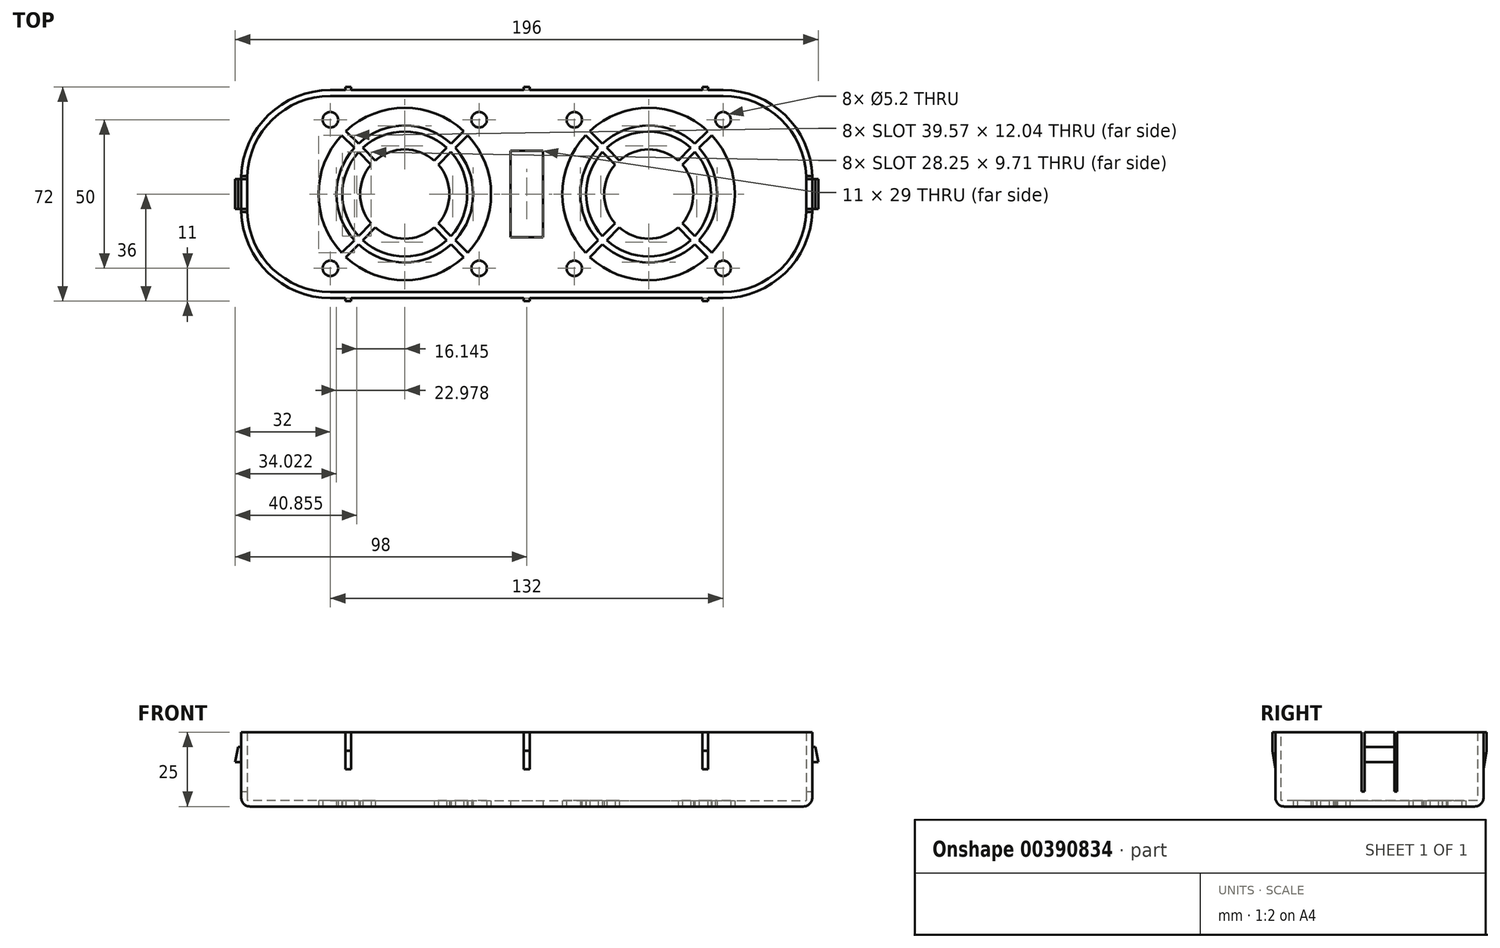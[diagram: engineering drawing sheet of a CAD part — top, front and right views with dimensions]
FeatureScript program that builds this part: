
annotation { "Feature Type Name" : "Feature", "Feature Type Description" : "" }
export const myFeature = defineFeature(function(context is Context, id is Id, definition is map)
    precondition{}
    {
        {
            var Q0;
            Q0=qCreatedBy(makeId("Top.planeOp"),FACE);
            var sketch = newSketch(context, id + "F0", { "sketchPlane" : qUnion([Q0])});
            skLineSegment(sketch, "E0", {"start": v(-96, 0) * mm, "end": v(96, 0) * mm, "construction": true});
            skLineSegment(sketch, "E1", {"start": v(0, 35) * mm, "end": v(0, -35) * mm, "construction": true});
            skLineSegment(sketch, "E2", {"start": v(-96, 5) * mm, "end": v(-96, -5) * mm});
            skArc(sketch, "E3", {"start": v(-96, 5) * mm, "mid": v(-87.21, 26.21) * mm, "end": v(-66, 35) * mm});
            skArc(sketch, "E4", {"start": v(-96, -5) * mm, "mid": v(-87.21, -26.21) * mm, "end": v(-66, -35) * mm});
            skLineSegment(sketch, "E5", {"start": v(96, 5) * mm, "end": v(96, -5) * mm});
            skArc(sketch, "E6", {"start": v(96, 5) * mm, "mid": v(87.21, 26.21) * mm, "end": v(66, 35) * mm});
            skArc(sketch, "E7", {"start": v(96, -5) * mm, "mid": v(87.21, -26.21) * mm, "end": v(66, -35) * mm});
            skLineSegment(sketch, "E8", {"start": v(-66, 35) * mm, "end": v(66, 35) * mm});
            skLineSegment(sketch, "E9", {"start": v(-66, -35) * mm, "end": v(66, -35) * mm});
            skSolve(sketch);
        }
        {
            var Q0;
            Q0 = qSketchRegion(id + "F0", true);
            extrude(context, id + "F1", {"entities" : qUnion([Q0]), "depth" : 25 * mm});
        }
        {
            var Q0;
            Q0=makeQuery(id+"F1.opExtrude","CAP_FACE",FACE,{"disambiguationData":[OSD([sQuery(id+"F0.wireOp",EDGE,"E2"),sQuery(id+"F0.wireOp",EDGE,"E3"),sQuery(id+"F0.wireOp",EDGE,"E4"),sQuery(id+"F0.wireOp",EDGE,"E5"),sQuery(id+"F0.wireOp",EDGE,"E6"),sQuery(id+"F0.wireOp",EDGE,"E7"),sQuery(id+"F0.wireOp",EDGE,"E8"),sQuery(id+"F0.wireOp",EDGE,"E9")])],"isStart":false});
            shell(context, id + "F2", {"entities" : qUnion([Q0]), "thickness" : 2 * mm});
        }
        {
            var Q0;
            Q0=makeQuery(id+"F1.opExtrude","SWEPT_FACE",FACE,{"disambiguationData":[OSD([sQuery(id+"F0.wireOp",EDGE,"E5")])]});
            var sketch = newSketch(context, id + "F3", { "sketchPlane" : qUnion([Q0])});
            skLineSegment(sketch, "E10", {"start": v(-5, 25) * mm, "end": v(-5, 5) * mm});
            skLineSegment(sketch, "E11", {"start": v(5, 5) * mm, "end": v(5, 25) * mm});
            skLineSegment(sketch, "E12", {"start": v(5, 25) * mm, "end": v(6, 25) * mm});
            skLineSegment(sketch, "E13", {"start": v(6, 25) * mm, "end": v(6, 5) * mm});
            skLineSegment(sketch, "E14", {"start": v(6, 5) * mm, "end": v(5, 5) * mm});
            skLineSegment(sketch, "E15", {"start": v(-5, 25) * mm, "end": v(-6, 25) * mm});
            skLineSegment(sketch, "E16", {"start": v(-6, 25) * mm, "end": v(-6, 5) * mm});
            skLineSegment(sketch, "E17", {"start": v(-6, 5) * mm, "end": v(-5, 5) * mm});
            skSolve(sketch);
        }
        {
            var Q0;
            Q0 = qSketchRegion(id + "F3", true);
            extrude(context, id + "F4", {"entities" : qUnion([Q0]), "operationType" : NewBodyOperationType.REMOVE, "endBound" : BoundingType.THROUGH_ALL, "oppositeDirection" : true, "depth" : 25 * mm});
        }
        {
            var Q0;
            Q0=makeQuery(id+"F1.opExtrude","SWEPT_FACE",FACE,{"disambiguationData":[OSD([sQuery(id+"F0.wireOp",EDGE,"E5")])]});
            var sketch = newSketch(context, id + "F5", { "sketchPlane" : qUnion([Q0])});
            skLineSegment(sketch, "E18.bottom", {"start": v(-5, 20) * mm, "end": v(5, 20) * mm});
            skLineSegment(sketch, "E18.top", {"start": v(-5, 15) * mm, "end": v(5, 15) * mm});
            skLineSegment(sketch, "E18.left", {"start": v(-5, 20) * mm, "end": v(-5, 15) * mm});
            skLineSegment(sketch, "E18.right", {"start": v(5, 20) * mm, "end": v(5, 15) * mm});
            skSolve(sketch);
        }
        {
            var Q0;
            Q0 = qSketchRegion(id + "F5", true);
            extrude(context, id + "F6", {"entities" : qUnion([Q0]), "operationType" : NewBodyOperationType.ADD, "depth" : 2 * mm});
        }
        {
            var Q0;
            {var subQ0=sQuery(id+"F0.wireOp",EDGE,"E5");Q0=makeQuery(id+"F6.boolean.opBoolean","MERGE",FACE,{"derivedFrom":[makeQuery(id+"F4.boolean.opBoolean","COPY",FACE,{"disambiguationData":[TD([makeQuery(id+"F1.opExtrude","SWEPT_FACE",FACE,{"disambiguationData":[OSD([subQ0])]})])],"derivedFrom":makeQuery(id+"F4.opExtrude","SWEPT_FACE",FACE,{"disambiguationData":[OSD([sQuery(id+"F3.wireOp",EDGE,"E10")])]})}),makeQuery(id+"F6.opExtrude","SWEPT_FACE",FACE,{"disambiguationData":[OSD([sQuery(id+"F5.wireOp",EDGE,"E18.left")])]})]});}
            var sketch = newSketch(context, id + "F7", { "sketchPlane" : qUnion([Q0])});
            skLineSegment(sketch, "E19", {"start": v(98, 15) * mm, "end": v(97, 20) * mm});
            skLineSegment(sketch, "E20", {"start": v(97, 20) * mm, "end": v(98, 20) * mm});
            skLineSegment(sketch, "E21", {"start": v(98, 20) * mm, "end": v(98, 15) * mm});
            skSolve(sketch);
        }
        {
            var Q0;
            Q0 = qSketchRegion(id + "F7", true);
            extrude(context, id + "F8", {"entities" : qUnion([Q0]), "operationType" : NewBodyOperationType.REMOVE, "endBound" : BoundingType.THROUGH_ALL, "oppositeDirection" : true, "depth" : 25 * mm});
        }
        {
            var Q0;
            Q0=makeQuery(id+"F1.opExtrude","SWEPT_FACE",FACE,{"disambiguationData":[OSD([sQuery(id+"F0.wireOp",EDGE,"E2")])]});
            var sketch = newSketch(context, id + "F9", { "sketchPlane" : qUnion([Q0])});
            skLineSegment(sketch, "E22.bottom", {"start": v(-5, 20) * mm, "end": v(5, 20) * mm});
            skLineSegment(sketch, "E22.left", {"start": v(-5, 20) * mm, "end": v(-5, 15) * mm});
            skLineSegment(sketch, "E23", {"start": v(-5, 15) * mm, "end": v(5, 15) * mm});
            skLineSegment(sketch, "E24", {"start": v(5, 15) * mm, "end": v(5, 20) * mm});
            skSolve(sketch);
        }
        {
            var Q0;
            Q0 = qSketchRegion(id + "F9", true);
            extrude(context, id + "F10", {"entities" : qUnion([Q0]), "operationType" : NewBodyOperationType.ADD, "depth" : 2 * mm});
        }
        {
            var Q0;
            {var subQ0=sQuery(id+"F0.wireOp",EDGE,"E2");Q0=makeQuery(id+"F10.boolean.opBoolean","MERGE",FACE,{"derivedFrom":[makeQuery(id+"F4.boolean.opBoolean","COPY",FACE,{"disambiguationData":[TD([makeQuery(id+"F1.opExtrude","SWEPT_FACE",FACE,{"disambiguationData":[OSD([subQ0])]})])],"derivedFrom":makeQuery(id+"F4.opExtrude","SWEPT_FACE",FACE,{"disambiguationData":[OSD([sQuery(id+"F3.wireOp",EDGE,"E11")])]})}),makeQuery(id+"F10.opExtrude","SWEPT_FACE",FACE,{"disambiguationData":[OSD([sQuery(id+"F9.wireOp",EDGE,"E22.left")])]})]});}
            var sketch = newSketch(context, id + "F11", { "sketchPlane" : qUnion([Q0])});
            skLineSegment(sketch, "E25", {"start": v(98, 15) * mm, "end": v(97, 20) * mm});
            skLineSegment(sketch, "E26", {"start": v(97, 20) * mm, "end": v(98, 20) * mm});
            skLineSegment(sketch, "E27", {"start": v(98, 20) * mm, "end": v(98, 15) * mm});
            skSolve(sketch);
        }
        {
            var Q0;
            Q0 = qSketchRegion(id + "F11", true);
            extrude(context, id + "F12", {"entities" : qUnion([Q0]), "operationType" : NewBodyOperationType.REMOVE, "endBound" : BoundingType.THROUGH_ALL, "oppositeDirection" : true, "depth" : 25 * mm});
        }
        {
            var Q0;
            Q0=makeQuery(id+"F1.opExtrude","SWEPT_FACE",FACE,{"disambiguationData":[OSD([sQuery(id+"F0.wireOp",EDGE,"E8")])]});
            var sketch = newSketch(context, id + "F13", { "sketchPlane" : qUnion([Q0])});
            skPoint(sketch, "E28.oppositeSnap0", {"position": v(-66, 12.5) * mm});
            skLineSegment(sketch, "E28.bottom", {"start": v(-61, 25) * mm, "end": v(-59, 25) * mm});
            skLineSegment(sketch, "E28.top", {"start": v(-61, 12.5) * mm, "end": v(-59, 12.5) * mm});
            skLineSegment(sketch, "E28.left", {"start": v(-61, 25) * mm, "end": v(-61, 12.5) * mm});
            skLineSegment(sketch, "E28.right", {"start": v(-59, 25) * mm, "end": v(-59, 12.5) * mm});
            skLineSegment(sketch, "E29.bottom", {"start": v(-1, 12.5) * mm, "end": v(1, 12.5) * mm});
            skLineSegment(sketch, "E29.top", {"start": v(-1, 25) * mm, "end": v(1, 25) * mm});
            skLineSegment(sketch, "E29.left", {"start": v(-1, 12.5) * mm, "end": v(-1, 25) * mm});
            skLineSegment(sketch, "E29.right", {"start": v(1, 12.5) * mm, "end": v(1, 25) * mm});
            skLineSegment(sketch, "E30.bottom", {"start": v(61, 25) * mm, "end": v(59, 25) * mm});
            skLineSegment(sketch, "E30.top", {"start": v(61, 12.5) * mm, "end": v(59, 12.5) * mm});
            skLineSegment(sketch, "E30.left", {"start": v(61, 25) * mm, "end": v(61, 12.5) * mm});
            skLineSegment(sketch, "E30.right", {"start": v(59, 25) * mm, "end": v(59, 12.5) * mm});
            skSolve(sketch);
        }
        {
            var Q0;
            Q0 = qSketchRegion(id + "F13", true);
            extrude(context, id + "F14", {"entities" : qUnion([Q0]), "operationType" : NewBodyOperationType.ADD, "depth" : 1 * mm});
        }
        {
            var Q0;
            Q0=makeQuery(id+"F14.opExtrude","SWEPT_FACE",FACE,{"disambiguationData":[OSD([sQuery(id+"F13.wireOp",EDGE,"E30.left")])]});
            var sketch = newSketch(context, id + "F15", { "sketchPlane" : qUnion([Q0])});
            skLineSegment(sketch, "E31", {"start": v(-35, 12.5) * mm, "end": v(-36, 18.75) * mm});
            skLineSegment(sketch, "E32", {"start": v(-36, 18.75) * mm, "end": v(-36, 12.5) * mm});
            skLineSegment(sketch, "E33", {"start": v(-36, 12.5) * mm, "end": v(-35, 12.5) * mm});
            skSolve(sketch);
        }
        {
            var Q0;
            Q0 = qSketchRegion(id + "F15", true);
            extrude(context, id + "F16", {"entities" : qUnion([Q0]), "operationType" : NewBodyOperationType.REMOVE, "endBound" : BoundingType.THROUGH_ALL, "oppositeDirection" : true, "depth" : 25 * mm});
        }
        {
            var Q0;
            Q0=makeQuery(id+"F1.opExtrude","SWEPT_FACE",FACE,{"disambiguationData":[OSD([sQuery(id+"F0.wireOp",EDGE,"E9")])]});
            var sketch = newSketch(context, id + "F17", { "sketchPlane" : qUnion([Q0])});
            skPoint(sketch, "E34.oppositeSnap0", {"position": v(-66, 12.5) * mm});
            skLineSegment(sketch, "E34.bottom", {"start": v(-61, 25) * mm, "end": v(-59, 25) * mm});
            skLineSegment(sketch, "E34.top", {"start": v(-61, 12.5) * mm, "end": v(-59, 12.5) * mm});
            skLineSegment(sketch, "E34.left", {"start": v(-61, 25) * mm, "end": v(-61, 12.5) * mm});
            skLineSegment(sketch, "E34.right", {"start": v(-59, 25) * mm, "end": v(-59, 12.5) * mm});
            skLineSegment(sketch, "E35.bottom", {"start": v(-1, 25) * mm, "end": v(1, 25) * mm});
            skLineSegment(sketch, "E35.top", {"start": v(-1, 12.5) * mm, "end": v(1, 12.5) * mm});
            skLineSegment(sketch, "E35.left", {"start": v(-1, 25) * mm, "end": v(-1, 12.5) * mm});
            skLineSegment(sketch, "E35.right", {"start": v(1, 25) * mm, "end": v(1, 12.5) * mm});
            skLineSegment(sketch, "E36.bottom", {"start": v(61, 25) * mm, "end": v(59, 25) * mm});
            skLineSegment(sketch, "E36.top", {"start": v(61, 12.5) * mm, "end": v(59, 12.5) * mm});
            skLineSegment(sketch, "E36.left", {"start": v(61, 25) * mm, "end": v(61, 12.5) * mm});
            skLineSegment(sketch, "E36.right", {"start": v(59, 25) * mm, "end": v(59, 12.5) * mm});
            skSolve(sketch);
        }
        {
            var Q0;
            Q0 = qSketchRegion(id + "F17", true);
            extrude(context, id + "F18", {"entities" : qUnion([Q0]), "operationType" : NewBodyOperationType.ADD, "depth" : 1 * mm});
        }
        {
            var Q0;
            Q0=makeQuery(id+"F18.opExtrude","SWEPT_FACE",FACE,{"disambiguationData":[OSD([sQuery(id+"F17.wireOp",EDGE,"E36.left")])]});
            var sketch = newSketch(context, id + "F19", { "sketchPlane" : qUnion([Q0])});
            skLineSegment(sketch, "E37", {"start": v(-35, 12.5) * mm, "end": v(-36, 18.75) * mm});
            skLineSegment(sketch, "E38", {"start": v(-36, 18.75) * mm, "end": v(-36, 12.5) * mm});
            skLineSegment(sketch, "E39", {"start": v(-36, 12.5) * mm, "end": v(-35, 12.5) * mm});
            skSolve(sketch);
        }
        {
            var Q0;
            Q0 = qSketchRegion(id + "F19", true);
            extrude(context, id + "F20", {"entities" : qUnion([Q0]), "operationType" : NewBodyOperationType.REMOVE, "endBound" : BoundingType.THROUGH_ALL, "oppositeDirection" : true, "depth" : 25 * mm});
        }
        {
            var Q0;
            Q0=makeQuery(id+"F1.opExtrude","CAP_FACE",FACE,{"disambiguationData":[OSD([sQuery(id+"F0.wireOp",EDGE,"E2"),sQuery(id+"F0.wireOp",EDGE,"E3"),sQuery(id+"F0.wireOp",EDGE,"E4"),sQuery(id+"F0.wireOp",EDGE,"E5"),sQuery(id+"F0.wireOp",EDGE,"E6"),sQuery(id+"F0.wireOp",EDGE,"E7"),sQuery(id+"F0.wireOp",EDGE,"E8"),sQuery(id+"F0.wireOp",EDGE,"E9")])],"isStart":true});
            var sketch = newSketch(context, id + "F21", { "sketchPlane" : qUnion([Q0])});
            skLineSegment(sketch, "E40.bottom", {"start": v(-16, 25) * mm, "end": v(-66, 25) * mm, "construction": true});
            skLineSegment(sketch, "E40.top", {"start": v(-16, -25) * mm, "end": v(-66, -25) * mm, "construction": true});
            skLineSegment(sketch, "E40.left", {"start": v(-16, 25) * mm, "end": v(-16, -25) * mm, "construction": true});
            skLineSegment(sketch, "E40.right", {"start": v(-66, 25) * mm, "end": v(-66, -25) * mm, "construction": true});
            skCircle(sketch, "E41", {"center": v(-66, 25) * mm, "radius": 2.6 * mm});
            skCircle(sketch, "E42", {"center": v(-16, 25) * mm, "radius": 2.6 * mm});
            skCircle(sketch, "E43", {"center": v(-66, -25) * mm, "radius": 2.6 * mm});
            skCircle(sketch, "E44", {"center": v(-16, -25) * mm, "radius": 2.6 * mm});
            skPoint(sketch, "E45.centerSnap0", {"position": v(-16, 0) * mm});
            skPoint(sketch, "E45.centerSnap1", {"position": v(-41, 25) * mm});
            skArc(sketch, "E46", {"start": v(-26.87, 15.54) * mm, "mid": v(-41, 21) * mm, "end": v(-55.13, 15.54) * mm});
            skArc(sketch, "E47", {"start": v(-25.46, 14.13) * mm, "mid": v(-20, 0) * mm, "end": v(-25.46, -14.13) * mm});
            skArc(sketch, "E48", {"start": v(-26.87, -15.54) * mm, "mid": v(-41, -21) * mm, "end": v(-55.13, -15.54) * mm});
            skArc(sketch, "E49", {"start": v(-56.54, -14.13) * mm, "mid": v(-62, 0) * mm, "end": v(-56.54, 14.13) * mm});
            skArc(sketch, "E50", {"start": v(-50.88, 11.3) * mm, "mid": v(-41, 15) * mm, "end": v(-31.12, 11.3) * mm});
            skArc(sketch, "E51", {"start": v(-29.7, 9.88) * mm, "mid": v(-26, 0) * mm, "end": v(-29.7, -9.88) * mm});
            skArc(sketch, "E52", {"start": v(-31.12, -11.3) * mm, "mid": v(-41, -15) * mm, "end": v(-50.88, -11.3) * mm});
            skArc(sketch, "E53", {"start": v(-52.3, -9.88) * mm, "mid": v(-56, 0) * mm, "end": v(-52.3, 9.88) * mm});
            skLineSegment(sketch, "E54", {"start": v(-55.13, 15.54) * mm, "end": v(-50.88, 11.3) * mm});
            skLineSegment(sketch, "E55", {"start": v(-52.3, 9.88) * mm, "end": v(-56.54, 14.13) * mm});
            skLineSegment(sketch, "E56", {"start": v(-31.12, 11.3) * mm, "end": v(-26.87, 15.54) * mm});
            skLineSegment(sketch, "E57", {"start": v(-25.46, 14.13) * mm, "end": v(-29.7, 9.88) * mm});
            skLineSegment(sketch, "E58", {"start": v(-29.7, -9.88) * mm, "end": v(-25.46, -14.13) * mm});
            skLineSegment(sketch, "E59", {"start": v(-26.87, -15.54) * mm, "end": v(-31.12, -11.3) * mm});
            skLineSegment(sketch, "E60", {"start": v(-50.88, -11.3) * mm, "end": v(-55.13, -15.54) * mm});
            skLineSegment(sketch, "E61", {"start": v(-56.54, -14.13) * mm, "end": v(-52.3, -9.88) * mm});
            skLineSegment(sketch, "E62", {"start": v(-66, 25) * mm, "end": v(-16, -25) * mm, "construction": true});
            skLineSegment(sketch, "E63", {"start": v(-16, 25) * mm, "end": v(-66, -25) * mm, "construction": true});
            skArc(sketch, "E64", {"start": v(-56.54, 16.96) * mm, "mid": v(-41, 23) * mm, "end": v(-25.46, 16.96) * mm});
            skArc(sketch, "E65", {"start": v(-60.79, 21.2) * mm, "mid": v(-41, 29) * mm, "end": v(-21.21, 21.2) * mm});
            skLineSegment(sketch, "E66", {"start": v(-60.79, 21.2) * mm, "end": v(-56.54, 16.96) * mm});
            skLineSegment(sketch, "E67", {"start": v(-25.46, 16.96) * mm, "end": v(-21.21, 21.2) * mm});
            skArc(sketch, "E68", {"start": v(-25.46, -16.96) * mm, "mid": v(-41, -23) * mm, "end": v(-56.54, -16.96) * mm});
            skArc(sketch, "E69", {"start": v(-21.21, -21.2) * mm, "mid": v(-41, -29) * mm, "end": v(-60.79, -21.2) * mm});
            skLineSegment(sketch, "E70", {"start": v(-56.54, -16.96) * mm, "end": v(-60.79, -21.2) * mm});
            skLineSegment(sketch, "E71", {"start": v(-25.46, -16.96) * mm, "end": v(-21.21, -21.2) * mm});
            skArc(sketch, "E72", {"start": v(-57.96, -15.54) * mm, "mid": v(-64, 0) * mm, "end": v(-57.96, 15.54) * mm});
            skArc(sketch, "E73", {"start": v(-62.2, -19.79) * mm, "mid": v(-70, 0) * mm, "end": v(-62.2, 19.79) * mm});
            skLineSegment(sketch, "E74", {"start": v(-57.96, 15.54) * mm, "end": v(-62.2, 19.79) * mm});
            skLineSegment(sketch, "E75", {"start": v(-57.96, -15.54) * mm, "end": v(-62.2, -19.79) * mm});
            skArc(sketch, "E76", {"start": v(-24.04, 15.54) * mm, "mid": v(-18, 0) * mm, "end": v(-24.04, -15.54) * mm});
            skArc(sketch, "E77", {"start": v(-19.8, 19.79) * mm, "mid": v(-12, 0) * mm, "end": v(-19.8, -19.79) * mm});
            skLineSegment(sketch, "E78", {"start": v(-24.04, 15.54) * mm, "end": v(-19.8, 19.79) * mm});
            skLineSegment(sketch, "E79", {"start": v(-24.04, -15.54) * mm, "end": v(-19.8, -19.79) * mm});
            skLineSegment(sketch, "E80.bottom", {"start": v(66, 25) * mm, "end": v(16, 25) * mm, "construction": true});
            skLineSegment(sketch, "E80.top", {"start": v(66, -25) * mm, "end": v(16, -25) * mm, "construction": true});
            skLineSegment(sketch, "E80.left", {"start": v(66, 25) * mm, "end": v(66, -25) * mm, "construction": true});
            skLineSegment(sketch, "E80.right", {"start": v(16, 25) * mm, "end": v(16, -25) * mm, "construction": true});
            skCircle(sketch, "E81", {"center": v(16, 25) * mm, "radius": 2.6 * mm});
            skCircle(sketch, "E82", {"center": v(66, 25) * mm, "radius": 2.6 * mm});
            skCircle(sketch, "E83", {"center": v(16, -25) * mm, "radius": 2.6 * mm});
            skCircle(sketch, "E84", {"center": v(66, -25) * mm, "radius": 2.6 * mm});
            skPoint(sketch, "E85.centerSnap0", {"position": v(66, 0) * mm});
            skPoint(sketch, "E85.centerSnap1", {"position": v(41, 25) * mm});
            skArc(sketch, "E86", {"start": v(55.13, 15.54) * mm, "mid": v(41, 21) * mm, "end": v(26.87, 15.54) * mm});
            skArc(sketch, "E87", {"start": v(56.54, 14.13) * mm, "mid": v(62, 0) * mm, "end": v(56.54, -14.13) * mm});
            skArc(sketch, "E88", {"start": v(55.13, -15.54) * mm, "mid": v(41, -21) * mm, "end": v(26.87, -15.54) * mm});
            skArc(sketch, "E89", {"start": v(25.46, -14.13) * mm, "mid": v(20, 0) * mm, "end": v(25.46, 14.13) * mm});
            skArc(sketch, "E90", {"start": v(31.12, 11.3) * mm, "mid": v(41, 15) * mm, "end": v(50.88, 11.3) * mm});
            skArc(sketch, "E91", {"start": v(52.3, 9.88) * mm, "mid": v(56, 0) * mm, "end": v(52.3, -9.88) * mm});
            skArc(sketch, "E92", {"start": v(50.88, -11.3) * mm, "mid": v(41, -15) * mm, "end": v(31.12, -11.3) * mm});
            skArc(sketch, "E93", {"start": v(29.7, -9.88) * mm, "mid": v(26, 0) * mm, "end": v(29.7, 9.88) * mm});
            skLineSegment(sketch, "E94", {"start": v(26.87, 15.54) * mm, "end": v(31.12, 11.3) * mm});
            skLineSegment(sketch, "E95", {"start": v(29.7, 9.88) * mm, "end": v(25.46, 14.13) * mm});
            skLineSegment(sketch, "E96", {"start": v(50.88, 11.3) * mm, "end": v(55.13, 15.54) * mm});
            skLineSegment(sketch, "E97", {"start": v(56.54, 14.13) * mm, "end": v(52.3, 9.88) * mm});
            skLineSegment(sketch, "E98", {"start": v(52.3, -9.88) * mm, "end": v(56.54, -14.13) * mm});
            skLineSegment(sketch, "E99", {"start": v(55.13, -15.54) * mm, "end": v(50.88, -11.3) * mm});
            skLineSegment(sketch, "E100", {"start": v(31.12, -11.3) * mm, "end": v(26.87, -15.54) * mm});
            skLineSegment(sketch, "E101", {"start": v(25.46, -14.13) * mm, "end": v(29.7, -9.88) * mm});
            skLineSegment(sketch, "E102", {"start": v(16, 25) * mm, "end": v(66, -25) * mm, "construction": true});
            skLineSegment(sketch, "E103", {"start": v(66, 25) * mm, "end": v(16, -25) * mm, "construction": true});
            skArc(sketch, "E104", {"start": v(25.46, 16.96) * mm, "mid": v(41, 23) * mm, "end": v(56.54, 16.96) * mm});
            skArc(sketch, "E105", {"start": v(21.21, 21.2) * mm, "mid": v(41, 29) * mm, "end": v(60.79, 21.2) * mm});
            skLineSegment(sketch, "E106", {"start": v(21.21, 21.2) * mm, "end": v(25.46, 16.96) * mm});
            skLineSegment(sketch, "E107", {"start": v(56.54, 16.96) * mm, "end": v(60.79, 21.2) * mm});
            skArc(sketch, "E108", {"start": v(56.54, -16.96) * mm, "mid": v(41, -23) * mm, "end": v(25.46, -16.96) * mm});
            skArc(sketch, "E109", {"start": v(60.79, -21.2) * mm, "mid": v(41, -29) * mm, "end": v(21.21, -21.2) * mm});
            skLineSegment(sketch, "E110", {"start": v(25.46, -16.96) * mm, "end": v(21.21, -21.2) * mm});
            skLineSegment(sketch, "E111", {"start": v(56.54, -16.96) * mm, "end": v(60.79, -21.2) * mm});
            skArc(sketch, "E112", {"start": v(24.04, -15.54) * mm, "mid": v(18, 0) * mm, "end": v(24.04, 15.54) * mm});
            skArc(sketch, "E113", {"start": v(19.8, -19.79) * mm, "mid": v(12, 0) * mm, "end": v(19.8, 19.79) * mm});
            skLineSegment(sketch, "E114", {"start": v(24.04, 15.54) * mm, "end": v(19.8, 19.79) * mm});
            skLineSegment(sketch, "E115", {"start": v(24.04, -15.54) * mm, "end": v(19.8, -19.79) * mm});
            skArc(sketch, "E116", {"start": v(57.96, 15.54) * mm, "mid": v(64, 0) * mm, "end": v(57.96, -15.54) * mm});
            skArc(sketch, "E117", {"start": v(62.2, 19.79) * mm, "mid": v(70, 0) * mm, "end": v(62.2, -19.79) * mm});
            skLineSegment(sketch, "E118", {"start": v(57.96, 15.54) * mm, "end": v(62.2, 19.79) * mm});
            skLineSegment(sketch, "E119", {"start": v(57.96, -15.54) * mm, "end": v(62.2, -19.79) * mm});
            skSolve(sketch);
        }
        {
            var Q0;
            Q0 = qSketchRegion(id + "F21", true);
            extrude(context, id + "F22", {"entities" : qUnion([Q0]), "operationType" : NewBodyOperationType.REMOVE, "endBound" : BoundingType.THROUGH_ALL, "oppositeDirection" : true, "depth" : 25 * mm});
        }
        {
            var Q0;
            Q0=makeQuery(id+"F1.opExtrude","CAP_FACE",FACE,{"disambiguationData":[OSD([sQuery(id+"F0.wireOp",EDGE,"E2"),sQuery(id+"F0.wireOp",EDGE,"E3"),sQuery(id+"F0.wireOp",EDGE,"E4"),sQuery(id+"F0.wireOp",EDGE,"E5"),sQuery(id+"F0.wireOp",EDGE,"E6"),sQuery(id+"F0.wireOp",EDGE,"E7"),sQuery(id+"F0.wireOp",EDGE,"E8"),sQuery(id+"F0.wireOp",EDGE,"E9")])],"isStart":true});
            var sketch = newSketch(context, id + "F23", { "sketchPlane" : qUnion([Q0])});
            skLineSegment(sketch, "E120.bottom", {"start": v(5.5, 14.5) * mm, "end": v(-5.5, 14.5) * mm});
            skLineSegment(sketch, "E120.top", {"start": v(5.5, -14.5) * mm, "end": v(-5.5, -14.5) * mm});
            skLineSegment(sketch, "E120.left", {"start": v(5.5, 14.5) * mm, "end": v(5.5, -14.5) * mm});
            skLineSegment(sketch, "E120.right", {"start": v(-5.5, 14.5) * mm, "end": v(-5.5, -14.5) * mm});
            skPoint(sketch, "E120.middle", {"position": v(0, 0) * mm});
            skSolve(sketch);
        }
        {
            var Q0;
            Q0 = qSketchRegion(id + "F23", true);
            extrude(context, id + "F24", {"entities" : qUnion([Q0]), "operationType" : NewBodyOperationType.REMOVE, "endBound" : BoundingType.THROUGH_ALL, "oppositeDirection" : true, "depth" : 25 * mm});
        }
        {
            var Q0;
            Q0=makeQuery(id+"F1.opExtrude","CAP_EDGE",EDGE,{"disambiguationData":[OSD([sQuery(id+"F0.wireOp",EDGE,"E6")])],"isStart":true});
            fillet(context, id + "F25", {"entities" : qUnion([Q0]), "radius" : 3 * mm, "tangentPropagation" : true, "allowEdgeOverflow" : false});
        }
    });
